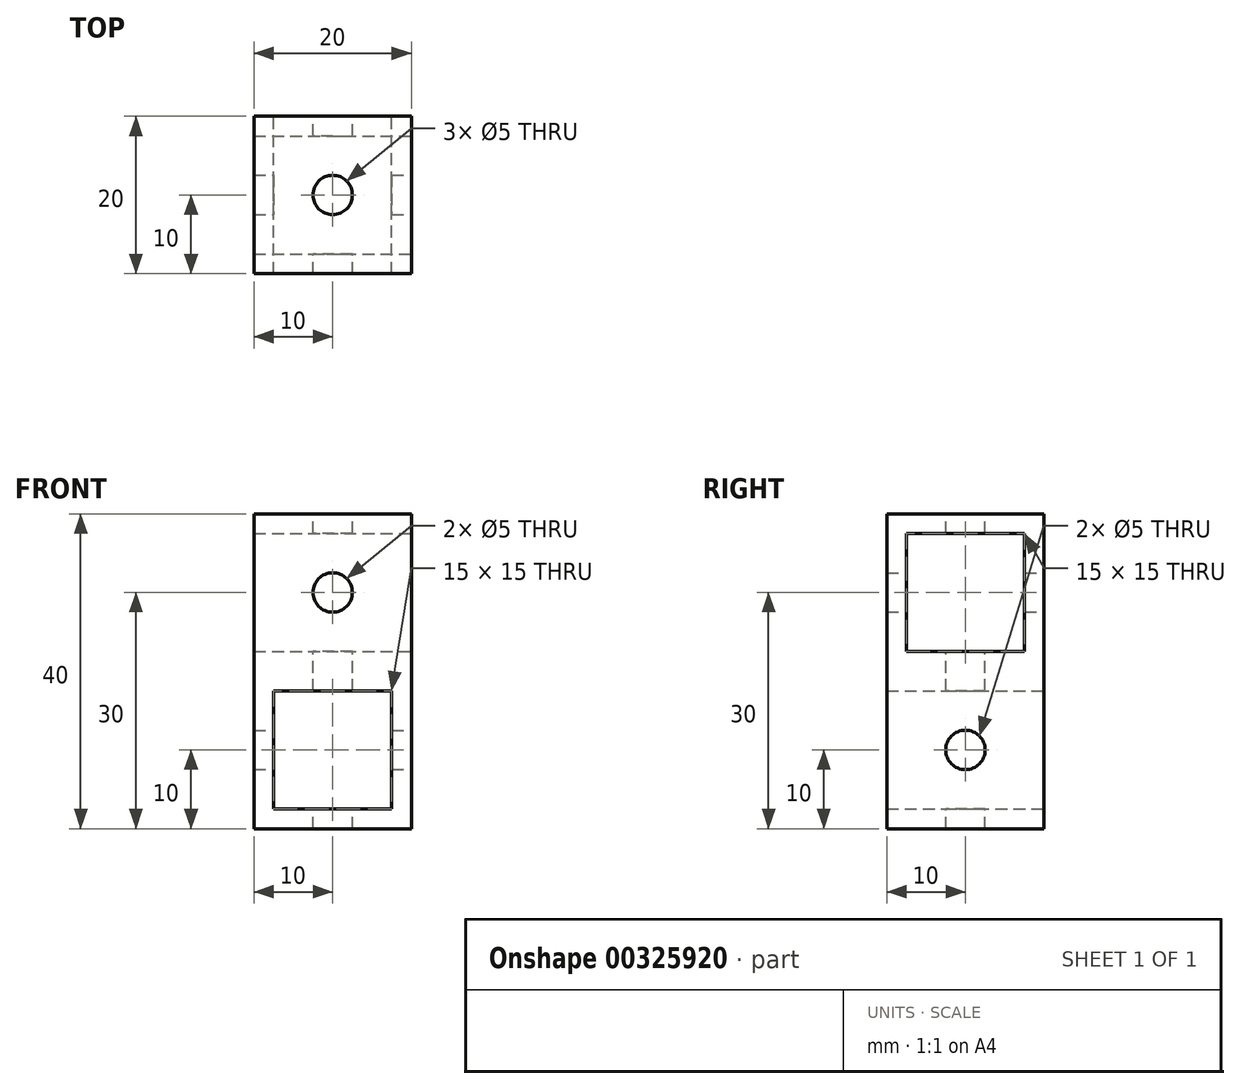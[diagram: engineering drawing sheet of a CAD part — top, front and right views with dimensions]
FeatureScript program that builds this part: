
annotation { "Feature Type Name" : "Feature", "Feature Type Description" : "" }
export const myFeature = defineFeature(function(context is Context, id is Id, definition is map)
    precondition{}
    {
        {
            var Q0;
            Q0=qCreatedBy(makeId("Front.planeOp"),FACE);
            var sketch = newSketch(context, id + "F0", { "sketchPlane" : qUnion([Q0])});
            skLineSegment(sketch, "E0.bottom", {"start": v(10, 20) * mm, "end": v(-10, 20) * mm});
            skLineSegment(sketch, "E0.top", {"start": v(10, -20) * mm, "end": v(-10, -20) * mm});
            skLineSegment(sketch, "E0.left", {"start": v(10, 20) * mm, "end": v(10, -20) * mm});
            skLineSegment(sketch, "E0.right", {"start": v(-10, 20) * mm, "end": v(-10, -20) * mm});
            skPoint(sketch, "E0.middle", {"position": v(0, 0) * mm});
            skSolve(sketch);
        }
        {
            var Q0;
            Q0 = qSketchRegion(id + "F0", true);
            extrude(context, id + "F1", {"entities" : qUnion([Q0]), "depth" : 20 * mm});
        }
        {
            var Q0;
            Q0=makeQuery(id+"F1.opExtrude","SWEPT_FACE",FACE,{"disambiguationData":[OSD([sQuery(id+"F0.wireOp",EDGE,"E0.left")])]});
            var sketch = newSketch(context, id + "F2", { "sketchPlane" : qUnion([Q0])});
            skLineSegment(sketch, "E1.bottom", {"start": v(-20, 20) * mm, "end": v(0, 20) * mm, "construction": true});
            skLineSegment(sketch, "E1.top", {"start": v(-20, 0) * mm, "end": v(0, 0) * mm, "construction": true});
            skLineSegment(sketch, "E1.left", {"start": v(-20, 20) * mm, "end": v(-20, 0) * mm, "construction": true});
            skLineSegment(sketch, "E1.right", {"start": v(0, 20) * mm, "end": v(0, 0) * mm, "construction": true});
            skLineSegment(sketch, "E2.bottom", {"start": v(0, -20) * mm, "end": v(-20, -20) * mm, "construction": true});
            skLineSegment(sketch, "E2.top", {"start": v(0, 0) * mm, "end": v(-20, 0) * mm, "construction": true});
            skLineSegment(sketch, "E2.left", {"start": v(0, -20) * mm, "end": v(0, 0) * mm, "construction": true});
            skLineSegment(sketch, "E2.right", {"start": v(-20, -20) * mm, "end": v(-20, 0) * mm, "construction": true});
            skLineSegment(sketch, "E3", {"start": v(-20, 20) * mm, "end": v(0, 0) * mm, "construction": true});
            skLineSegment(sketch, "E4", {"start": v(0, 20) * mm, "end": v(-20, 0) * mm, "construction": true});
            skLineSegment(sketch, "E5", {"start": v(-20, 0) * mm, "end": v(0, -20) * mm, "construction": true});
            skLineSegment(sketch, "E6", {"start": v(0, 0) * mm, "end": v(-20, -20) * mm, "construction": true});
            skLineSegment(sketch, "E7.bottom", {"start": v(-2.5, 17.5) * mm, "end": v(-17.5, 17.5) * mm});
            skLineSegment(sketch, "E7.top", {"start": v(-2.5, 2.5) * mm, "end": v(-17.5, 2.5) * mm});
            skLineSegment(sketch, "E7.left", {"start": v(-2.5, 17.5) * mm, "end": v(-2.5, 2.5) * mm});
            skLineSegment(sketch, "E7.right", {"start": v(-17.5, 17.5) * mm, "end": v(-17.5, 2.5) * mm});
            skPoint(sketch, "E7.middle", {"position": v(-10, 10) * mm});
            skCircle(sketch, "E8", {"center": v(-10, -10) * mm, "radius": 2.5 * mm});
            skSolve(sketch);
        }
        {
            var Q0;
            Q0 = qSketchRegion(id + "F2", true);
            extrude(context, id + "F3", {"entities" : qUnion([Q0]), "operationType" : NewBodyOperationType.REMOVE, "endBound" : BoundingType.THROUGH_ALL, "oppositeDirection" : true, "depth" : 25 * mm});
        }
        {
            var Q0;
            Q0=makeQuery(id+"F1.opExtrude","CAP_FACE",FACE,{"disambiguationData":[OSD([sQuery(id+"F0.wireOp",EDGE,"E0.bottom"),sQuery(id+"F0.wireOp",EDGE,"E0.top"),sQuery(id+"F0.wireOp",EDGE,"E0.left"),sQuery(id+"F0.wireOp",EDGE,"E0.right")])],"isStart":true});
            var sketch = newSketch(context, id + "F4", { "sketchPlane" : qUnion([Q0])});
            skLineSegment(sketch, "E9.bottom", {"start": v(10, -20) * mm, "end": v(-10, -20) * mm, "construction": true});
            skLineSegment(sketch, "E9.top", {"start": v(10, 0) * mm, "end": v(-10, 0) * mm, "construction": true});
            skLineSegment(sketch, "E9.left", {"start": v(10, -20) * mm, "end": v(10, 0) * mm, "construction": true});
            skLineSegment(sketch, "E9.right", {"start": v(-10, -20) * mm, "end": v(-10, 0) * mm, "construction": true});
            skLineSegment(sketch, "E10.bottom", {"start": v(-10, 0) * mm, "end": v(10, 0) * mm, "construction": true});
            skLineSegment(sketch, "E10.top", {"start": v(-10, 20) * mm, "end": v(10, 20) * mm, "construction": true});
            skLineSegment(sketch, "E10.left", {"start": v(-10, 0) * mm, "end": v(-10, 20) * mm, "construction": true});
            skLineSegment(sketch, "E10.right", {"start": v(10, 0) * mm, "end": v(10, 20) * mm, "construction": true});
            skLineSegment(sketch, "E11", {"start": v(10, -20) * mm, "end": v(-10, 0) * mm, "construction": true});
            skLineSegment(sketch, "E12", {"start": v(-10, -20) * mm, "end": v(10, 0) * mm, "construction": true});
            skLineSegment(sketch, "E13", {"start": v(-10, 20) * mm, "end": v(10, 0) * mm, "construction": true});
            skLineSegment(sketch, "E14", {"start": v(10, 20) * mm, "end": v(-10, 0) * mm, "construction": true});
            skLineSegment(sketch, "E15.bottom", {"start": v(7.5, -2.5) * mm, "end": v(-7.5, -2.5) * mm});
            skLineSegment(sketch, "E15.top", {"start": v(7.5, -17.5) * mm, "end": v(-7.5, -17.5) * mm});
            skLineSegment(sketch, "E15.left", {"start": v(7.5, -2.5) * mm, "end": v(7.5, -17.5) * mm});
            skLineSegment(sketch, "E15.right", {"start": v(-7.5, -2.5) * mm, "end": v(-7.5, -17.5) * mm});
            skPoint(sketch, "E15.middle", {"position": v(0, -10) * mm});
            skCircle(sketch, "E16", {"center": v(0, 10) * mm, "radius": 2.5 * mm});
            skSolve(sketch);
        }
        {
            var Q0;
            Q0 = qSketchRegion(id + "F4", true);
            extrude(context, id + "F5", {"entities" : qUnion([Q0]), "operationType" : NewBodyOperationType.REMOVE, "endBound" : BoundingType.THROUGH_ALL, "oppositeDirection" : true, "depth" : 25 * mm});
        }
        {
            var Q0;
            Q0=makeQuery(id+"F1.opExtrude","SWEPT_FACE",FACE,{"disambiguationData":[OSD([sQuery(id+"F0.wireOp",EDGE,"E0.bottom")])]});
            var sketch = newSketch(context, id + "F6", { "sketchPlane" : qUnion([Q0])});
            skLineSegment(sketch, "E17.bottom", {"start": v(-10, 0) * mm, "end": v(10, 0) * mm, "construction": true});
            skLineSegment(sketch, "E17.top", {"start": v(-10, -20) * mm, "end": v(10, -20) * mm, "construction": true});
            skLineSegment(sketch, "E17.left", {"start": v(-10, 0) * mm, "end": v(-10, -20) * mm, "construction": true});
            skLineSegment(sketch, "E17.right", {"start": v(10, 0) * mm, "end": v(10, -20) * mm, "construction": true});
            skLineSegment(sketch, "E18", {"start": v(-10, 0) * mm, "end": v(10, -20) * mm, "construction": true});
            skLineSegment(sketch, "E19", {"start": v(10, 0) * mm, "end": v(-10, -20) * mm, "construction": true});
            skCircle(sketch, "E20", {"center": v(0, -10) * mm, "radius": 2.5 * mm});
            skSolve(sketch);
        }
        {
            var Q0;
            Q0 = qSketchRegion(id + "F6", true);
            extrude(context, id + "F7", {"entities" : qUnion([Q0]), "operationType" : NewBodyOperationType.REMOVE, "endBound" : BoundingType.THROUGH_ALL, "oppositeDirection" : true, "depth" : 25 * mm});
        }
    });
